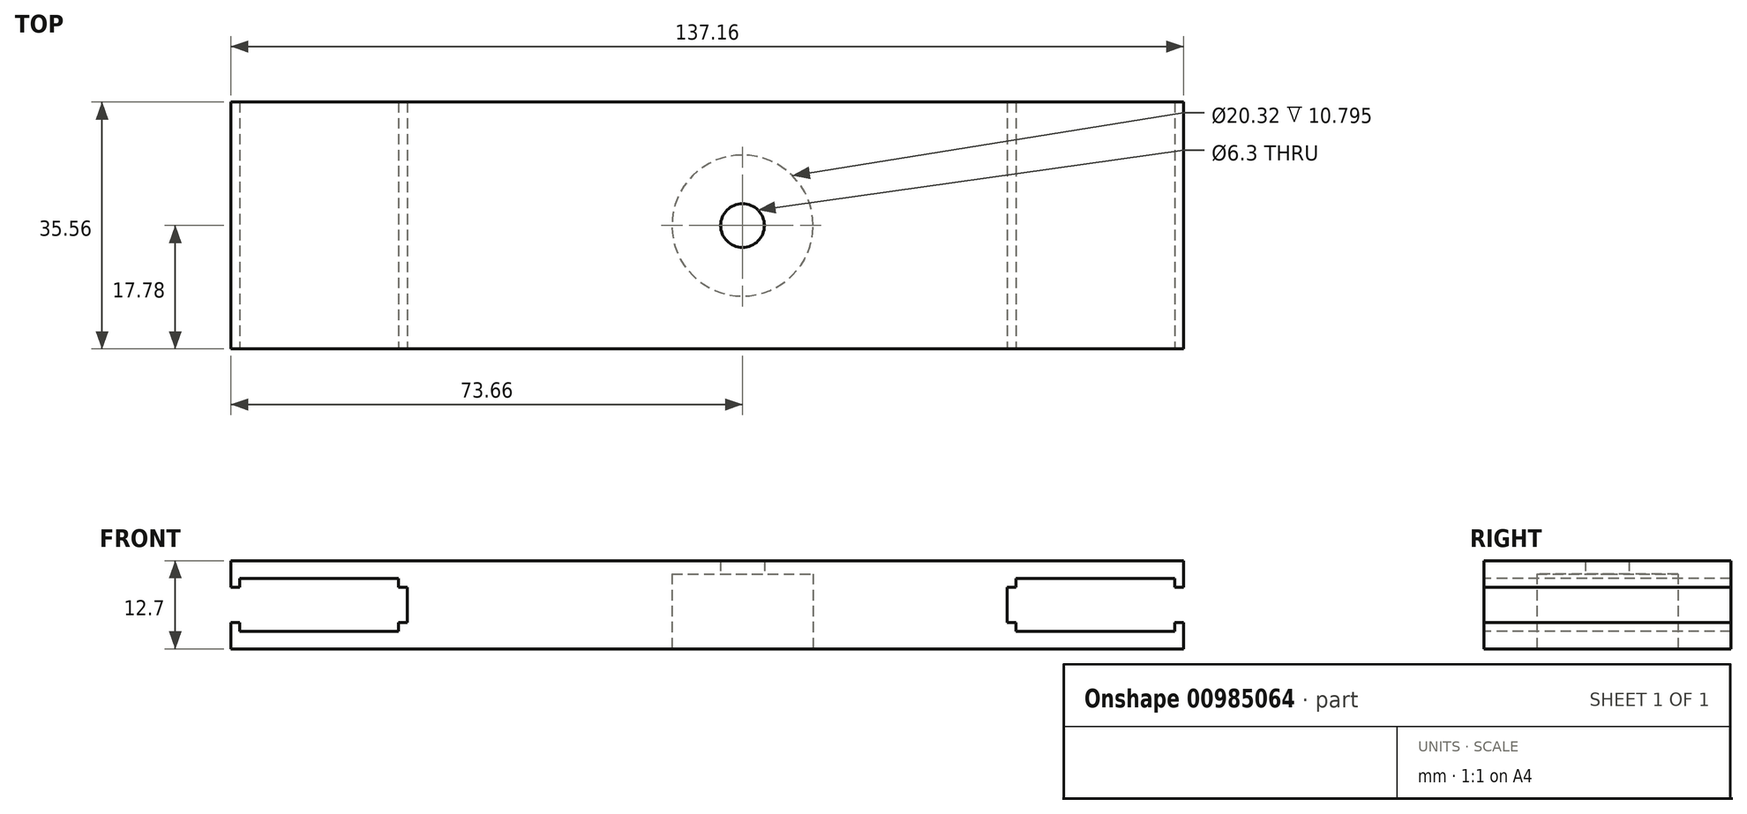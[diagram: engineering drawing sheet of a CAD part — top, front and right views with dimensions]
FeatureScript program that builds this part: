
annotation { "Feature Type Name" : "Feature", "Feature Type Description" : "" }
export const myFeature = defineFeature(function(context is Context, id is Id, definition is map)
    precondition{}
    {
        {
            var Q0;
            Q0=qCreatedBy(makeId("Top.planeOp"),FACE);
            var sketch = newSketch(context, id + "F0", { "sketchPlane" : qUnion([Q0])});
            skLineSegment(sketch, "E0.bottom", {"start": v(68.58, -17.78) * mm, "end": v(-68.58, -17.78) * mm});
            skLineSegment(sketch, "E0.top", {"start": v(68.58, 17.78) * mm, "end": v(-68.58, 17.78) * mm});
            skLineSegment(sketch, "E0.left", {"start": v(68.58, -17.78) * mm, "end": v(68.58, 17.78) * mm});
            skLineSegment(sketch, "E0.right", {"start": v(-68.58, -17.78) * mm, "end": v(-68.58, 17.78) * mm});
            skPoint(sketch, "E0.middle", {"position": v(0, 0) * mm});
            skSolve(sketch);
        }
        {
            var Q0;
            Q0=makeQuery(id+"F0.imprint","IMPRINT",FACE,{"disambiguationData":[TD([[makeQuery(id+"F0.imprint","IMPRINT",EDGE,{"derivedFrom":sQuery(id+"F0.wireOp",EDGE,"E0.bottom")}),-1.0]])]});
            extrude(context, id + "F1", {"entities" : qUnion([Q0]), "depth" : 12.7 * mm, "offsetDistance" : 25.4 * mm});
        }
        {
            var Q0;
            Q0=makeQuery(id+"F1.opExtrude","CAP_FACE",FACE,{"disambiguationData":[OSD([sQuery(id+"F0.wireOp",EDGE,"E0.bottom"),sQuery(id+"F0.wireOp",EDGE,"E0.top"),sQuery(id+"F0.wireOp",EDGE,"E0.left"),sQuery(id+"F0.wireOp",EDGE,"E0.right")])],"isStart":true});
            var sketch = newSketch(context, id + "F2", { "sketchPlane" : qUnion([Q0])});
            skCircle(sketch, "E1", {"center": v(5.08, 0) * mm, "radius": 10.16 * mm});
            skSolve(sketch);
        }
        {
            var Q0;
            Q0 = qSketchRegion(id + "F2", true);
            extrude(context, id + "F3", {"entities" : qUnion([Q0]), "operationType" : NewBodyOperationType.REMOVE, "oppositeDirection" : true, "depth" : 10.8 * mm, "offsetDistance" : 25.4 * mm});
        }
        {
            var Q0;
            Q0=makeQuery(id+"F3.boolean.opBoolean","COPY",FACE,{"derivedFrom":makeQuery(id+"F3.opExtrude","CAP_FACE",FACE,{"disambiguationData":[OSD([sQuery(id+"F2.wireOp",EDGE,"E1")])],"isStart":false})});
            var sketch = newSketch(context, id + "F4", { "sketchPlane" : qUnion([Q0])});
            skCircle(sketch, "E2", {"center": v(5.08, 0) * mm, "radius": 3.15 * mm});
            skSolve(sketch);
        }
        {
            var Q0;
            Q0=makeQuery(id+"F4.imprint","IMPRINT",FACE,{"disambiguationData":[TD([[makeQuery(id+"F4.imprint","IMPRINT",EDGE,{"derivedFrom":sQuery(id+"F4.wireOp",EDGE,"E2")}),1.0]])]});
            extrude(context, id + "F5", {"entities" : qUnion([Q0]), "operationType" : NewBodyOperationType.REMOVE, "oppositeDirection" : true, "depth" : 1.9 * mm, "offsetDistance" : 25.4 * mm});
        }
        {
            var Q0;
            Q0=makeQuery(id+"F1.opExtrude","SWEPT_FACE",FACE,{"disambiguationData":[OSD([sQuery(id+"F0.wireOp",EDGE,"E0.bottom")])]});
            var sketch = newSketch(context, id + "F6", { "sketchPlane" : qUnion([Q0])});
            skLineSegment(sketch, "E3.bottom", {"start": v(-68.58, 8.89) * mm, "end": v(-43.18, 8.9) * mm});
            skLineSegment(sketch, "E3.top", {"start": v(-68.58, 3.8) * mm, "end": v(-43.18, 3.81) * mm});
            skLineSegment(sketch, "E3.left", {"start": v(-68.58, 8.9) * mm, "end": v(-68.58, 3.81) * mm});
            skLineSegment(sketch, "E3.right", {"start": v(-43.18, 8.9) * mm, "end": v(-43.18, 3.81) * mm});
            skLineSegment(sketch, "E4.MirrorCS", {"start": v(68.58, 8.9) * mm, "end": v(68.58, 3.81) * mm});
            skLineSegment(sketch, "E5.MirrorCS", {"start": v(43.18, 8.9) * mm, "end": v(43.18, 3.81) * mm});
            skLineSegment(sketch, "E6.MirrorCS", {"start": v(68.58, 3.8) * mm, "end": v(43.18, 3.81) * mm});
            skLineSegment(sketch, "E7.MirrorCS", {"start": v(68.58, 8.89) * mm, "end": v(43.18, 8.9) * mm});
            skLineSegment(sketch, "E8.bottom", {"start": v(-67.31, 10.16) * mm, "end": v(-44.45, 10.16) * mm});
            skLineSegment(sketch, "E8.top", {"start": v(-67.31, 2.54) * mm, "end": v(-44.45, 2.54) * mm});
            skLineSegment(sketch, "E8.left", {"start": v(-67.31, 10.16) * mm, "end": v(-67.31, 2.54) * mm});
            skLineSegment(sketch, "E8.right", {"start": v(-44.45, 10.16) * mm, "end": v(-44.45, 2.54) * mm});
            skLineSegment(sketch, "E9.MirrorCS", {"start": v(67.31, 2.54) * mm, "end": v(44.45, 2.54) * mm});
            skLineSegment(sketch, "E10.MirrorCS", {"start": v(44.45, 10.16) * mm, "end": v(44.45, 2.54) * mm});
            skLineSegment(sketch, "E11.MirrorCS", {"start": v(67.31, 10.16) * mm, "end": v(44.45, 10.16) * mm});
            skLineSegment(sketch, "E12.MirrorCS", {"start": v(67.31, 10.16) * mm, "end": v(67.31, 2.54) * mm});
            skSolve(sketch);
        }
        {
            var Q0;
            {var subQ5=sQuery(id+"F6.wireOp",EDGE,"E9.MirrorCS");Q0=makeQuery(id+"F6.imprint","IMPRINT",FACE,{"disambiguationData":[TD([[makeQuery(id+"F6.imprint","IMPRINT",EDGE,{"derivedFrom":subQ5}),-1.0]])]});}
            var Q1;
            {var subQ0=sQuery(id+"F6.wireOp",EDGE,"E12.MirrorCS");var subQ1=sQuery(id+"F6.wireOp",EDGE,"E6.MirrorCS");var subQ2=makeQuery(id+"F6.imprint","INTERSECT",VERTEX,{"derivedFrom":[subQ1,subQ0]});Q1=makeQuery(id+"F6.imprint","IMPRINT",FACE,{"disambiguationData":[TD([[makeQuery(id+"F6.imprint","IMPRINT",EDGE,{"disambiguationData":[TD([[subQ2,-1.0]])],"derivedFrom":subQ1}),-1.0]])]});}
            var Q2;
            {var subQ0=sQuery(id+"F6.wireOp",EDGE,"E5.MirrorCS");Q2=makeQuery(id+"F6.imprint","IMPRINT",FACE,{"disambiguationData":[TD([[makeQuery(id+"F6.imprint","IMPRINT",EDGE,{"derivedFrom":subQ0}),1.0]])]});}
            var Q3;
            {var subQ5=sQuery(id+"F6.wireOp",EDGE,"E11.MirrorCS");Q3=makeQuery(id+"F6.imprint","IMPRINT",FACE,{"disambiguationData":[TD([[makeQuery(id+"F6.imprint","IMPRINT",EDGE,{"derivedFrom":subQ5}),1.0]])]});}
            var Q4;
            {var subQ0=sQuery(id+"F6.wireOp",EDGE,"E4.MirrorCS");Q4=makeQuery(id+"F6.imprint","IMPRINT",FACE,{"disambiguationData":[TD([[makeQuery(id+"F6.imprint","IMPRINT",EDGE,{"derivedFrom":subQ0}),-1.0]])]});}
            var Q5;
            {var subQ5=sQuery(id+"F6.wireOp",EDGE,"E8.top");Q5=makeQuery(id+"F6.imprint","IMPRINT",FACE,{"disambiguationData":[TD([[makeQuery(id+"F6.imprint","IMPRINT",EDGE,{"derivedFrom":subQ5}),1.0]])]});}
            var Q6;
            {var subQ0=sQuery(id+"F6.wireOp",EDGE,"E8.left");var subQ1=sQuery(id+"F6.wireOp",EDGE,"E3.bottom");var subQ2=makeQuery(id+"F6.imprint","INTERSECT",VERTEX,{"derivedFrom":[subQ1,subQ0]});Q6=makeQuery(id+"F6.imprint","IMPRINT",FACE,{"disambiguationData":[TD([[makeQuery(id+"F6.imprint","IMPRINT",EDGE,{"disambiguationData":[TD([[subQ2,-1.0]])],"derivedFrom":subQ1}),-1.0]])]});}
            var Q7;
            {var subQ0=sQuery(id+"F6.wireOp",EDGE,"E3.left");Q7=makeQuery(id+"F6.imprint","IMPRINT",FACE,{"disambiguationData":[TD([[makeQuery(id+"F6.imprint","IMPRINT",EDGE,{"derivedFrom":subQ0}),1.0]])]});}
            var Q8;
            {var subQ0=sQuery(id+"F6.wireOp",EDGE,"E3.right");Q8=makeQuery(id+"F6.imprint","IMPRINT",FACE,{"disambiguationData":[TD([[makeQuery(id+"F6.imprint","IMPRINT",EDGE,{"derivedFrom":subQ0}),-1.0]])]});}
            var Q9;
            {var subQ5=sQuery(id+"F6.wireOp",EDGE,"E8.bottom");Q9=makeQuery(id+"F6.imprint","IMPRINT",FACE,{"disambiguationData":[TD([[makeQuery(id+"F6.imprint","IMPRINT",EDGE,{"derivedFrom":subQ5}),-1.0]])]});}
            extrude(context, id + "F7", {"entities" : qUnion([Q0, Q1, Q2, Q3, Q4, Q5, Q6, Q7, Q8, Q9]), "operationType" : NewBodyOperationType.REMOVE, "oppositeDirection" : true, "depth" : 50.8 * mm, "offsetDistance" : 25.4 * mm});
        }
    });
